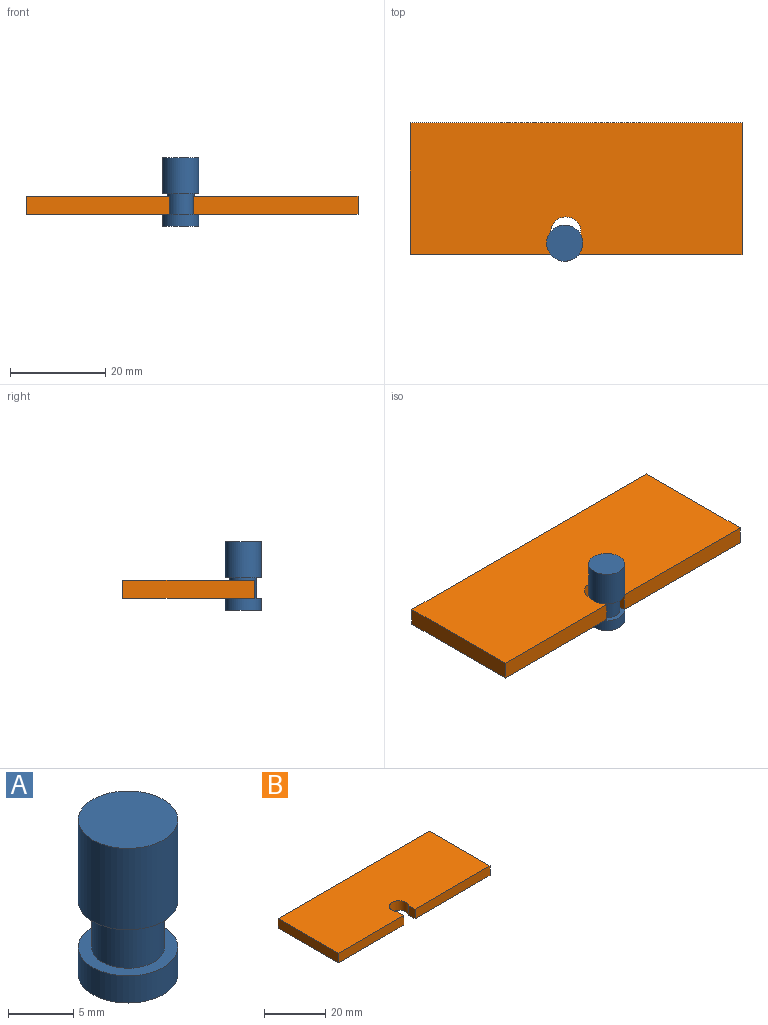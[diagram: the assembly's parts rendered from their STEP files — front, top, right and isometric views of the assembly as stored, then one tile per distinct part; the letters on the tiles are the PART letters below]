
ASSEMBLY  parts=2 mates=1
PART A: 7 faces, bbox 7.6x7.6x14.5 mm
  f0: cylinder r=3.81mm len=7.62mm, axis (0,0,-1), area 60.8mm2, adj f1,f2
  f1: plane 7.62x7.62mm, normal (0,0,1), area 21.1mm2, adj f0,f3
  f2: plane 7.62x7.62mm, normal (0,0,-1), area 45.6mm2, adj f0
  f3: cylinder r=2.79mm len=5.59mm, axis (0,0,-1), area 75.8mm2, adj f1,f6
  f4: cylinder r=3.81mm len=7.62mm, axis (0,0,-1), area 182.4mm2, adj f5,f6
  f5: plane 7.62x7.62mm, normal (0,0,1), area 45.6mm2, adj f4
  f6: plane 7.62x7.62mm, normal (0,0,-1), area 21.1mm2, adj f3,f4
PART B: 10 faces, bbox 69.9x27.8x3.8 mm
  f0: plane 34.53x3.81mm, normal (0,-1,0), area 131.5mm2, adj f3,f5,f6,f9
  f1: plane 27.77x3.81mm, normal (-1,0,0), area 105.8mm2, adj f2,f4,f5,f6
  f2: plane 30.25x3.81mm, normal (0,-1,0), area 115.3mm2, adj f1,f5,f6,f8
  f3: plane 27.77x3.81mm, normal (1,0,0), area 105.8mm2, adj f0,f4,f5,f6
  f4: plane 69.86x3.81mm, normal (0,1,0), area 266.2mm2, adj f1,f3,f5,f6
  f5: plane 69.86x27.77mm, normal (0,0,1), area 1898.7mm2, adj f0,f1,f2,f3,f4,f7,f8,f9
  f6: plane 69.86x27.77mm, normal (0,0,-1), area 1898.7mm2, adj f0,f1,f2,f3,f4,f7,f8,f9
  f7: cylinder r=3.17mm len=6.35mm, axis (0,0,1), area 53.6mm2, adj f5,f6,f8,f9
  f8: plane 3.81x2.85mm, normal (1,0,0), area 10.9mm2, adj f2,f5,f6,f7
  f9: plane 3.81x2.85mm, normal (-1,0,0), area 10.9mm2, adj f0,f5,f6,f7
PLACE A t=(-10.61,-13.36,-7.7)mm
PLACE B t=(-10.37,-0.06,-5.16)mm
MATE planar A.f0 <-> B.f6  axis (0,0,1) through (-10.61,-13.36,-5.16)mm
